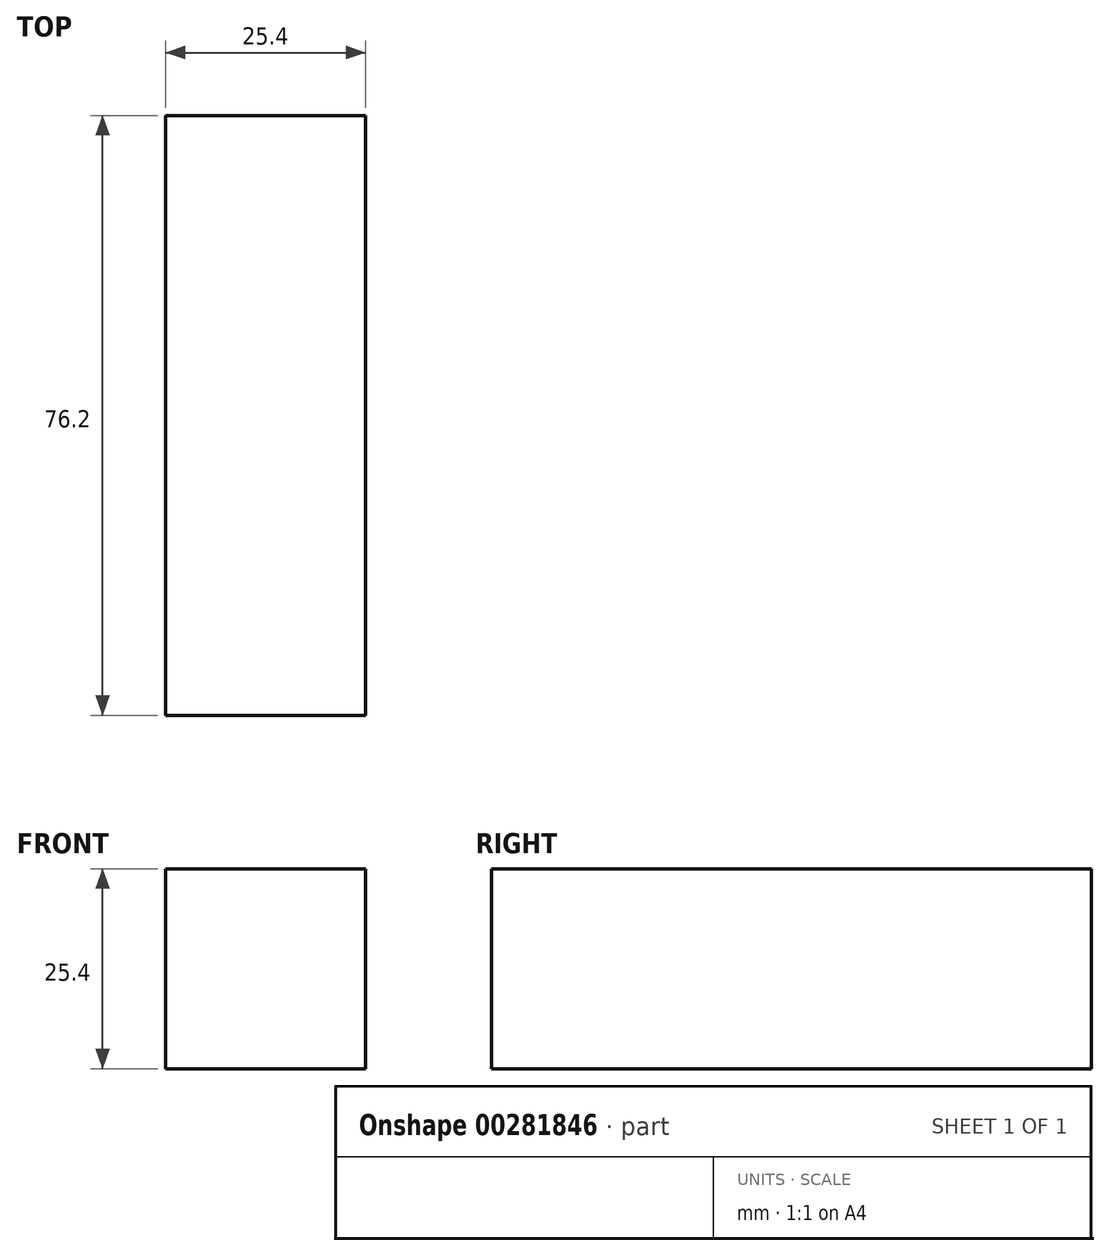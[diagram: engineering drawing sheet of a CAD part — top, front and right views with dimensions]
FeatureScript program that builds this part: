
annotation { "Feature Type Name" : "Feature", "Feature Type Description" : "" }
export const myFeature = defineFeature(function(context is Context, id is Id, definition is map)
    precondition{}
    {
        {
            var Q0;
            Q0=qCreatedBy(makeId("Front.planeOp"),FACE);
            var sketch = newSketch(context, id + "F0", { "sketchPlane" : qUnion([Q0])});
            skLineSegment(sketch, "E0.bottom", {"start": v(-2.1, 22.91) * mm, "end": v(-27.5, 22.91) * mm});
            skLineSegment(sketch, "E0.top", {"start": v(-2.1, 48.31) * mm, "end": v(-27.5, 48.31) * mm});
            skLineSegment(sketch, "E0.left", {"start": v(-2.1, 22.91) * mm, "end": v(-2.1, 48.31) * mm});
            skLineSegment(sketch, "E0.right", {"start": v(-27.5, 22.91) * mm, "end": v(-27.5, 48.31) * mm});
            skPoint(sketch, "E1.firstSnap0", {"position": v(-27.5, 35.61) * mm});
            skPoint(sketch, "E1.oppositeSnap0", {"position": v(-27.5, 35.61) * mm});
            skLineSegment(sketch, "E1.bottom", {"start": v(-17.57, 35.61) * mm, "end": v(-24.63, 35.61) * mm});
            skLineSegment(sketch, "E1.top", {"start": v(-17.57, 35.61) * mm, "end": v(-24.63, 35.61) * mm});
            skLineSegment(sketch, "E1.left", {"start": v(-17.57, 35.61) * mm, "end": v(-17.57, 35.61) * mm});
            skLineSegment(sketch, "E1.right", {"start": v(-24.63, 35.61) * mm, "end": v(-24.63, 35.61) * mm});
            skSolve(sketch);
        }
        {
            var Q0;
            Q0 = qSketchRegion(id + "F0", true);
            extrude(context, id + "F1", {"entities" : qUnion([Q0]), "depth" : 76.2 * mm});
        }
    });
